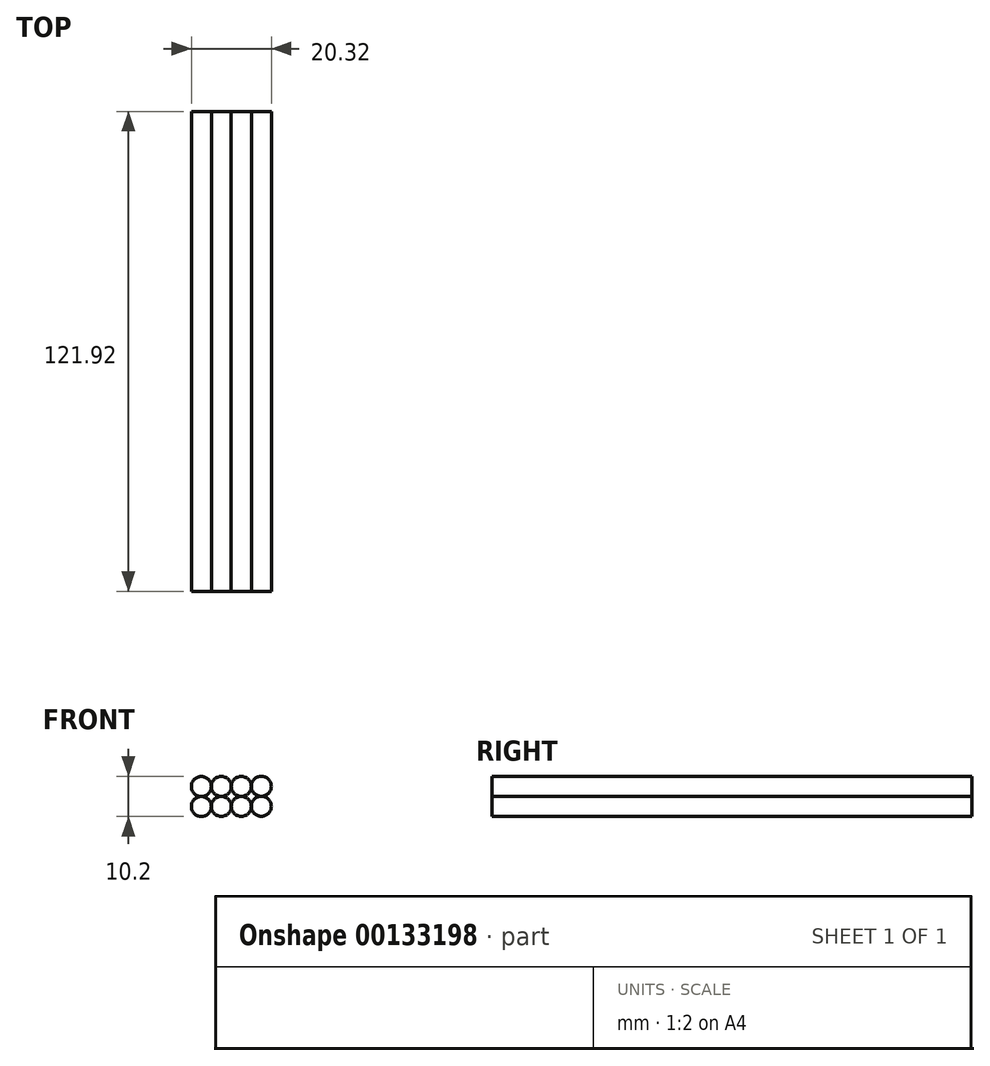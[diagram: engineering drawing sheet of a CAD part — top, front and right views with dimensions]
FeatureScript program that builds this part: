
annotation { "Feature Type Name" : "Feature", "Feature Type Description" : "" }
export const myFeature = defineFeature(function(context is Context, id is Id, definition is map)
    precondition{}
    {
        {
            var Q0;
            Q0=qCreatedBy(makeId("Front.planeOp"),FACE);
            var sketch = newSketch(context, id + "F0", { "sketchPlane" : qUnion([Q0])});
            skCircle(sketch, "E0", {"center": v(0, 0) * mm, "radius": 2.54 * mm});
            skCircle(sketch, "E1.0.1.0", {"center": v(0, 5.08) * mm, "radius": 2.54 * mm});
            skCircle(sketch, "E1.1.0.0", {"center": v(5.08, 0.01) * mm, "radius": 2.54 * mm});
            skCircle(sketch, "E1.1.1.0", {"center": v(5.08, 5.1) * mm, "radius": 2.54 * mm});
            skCircle(sketch, "E1.2.0.0", {"center": v(10.16, 0.02) * mm, "radius": 2.54 * mm});
            skCircle(sketch, "E1.2.1.0", {"center": v(10.16, 5.1) * mm, "radius": 2.54 * mm});
            skCircle(sketch, "E1.3.0.0", {"center": v(15.24, 0.04) * mm, "radius": 2.54 * mm});
            skCircle(sketch, "E1.3.1.0", {"center": v(15.24, 5.12) * mm, "radius": 2.54 * mm});
            skLineSegment(sketch, "E1.direction1", {"start": v(0, 0) * mm, "end": v(5.08, 0.01) * mm, "construction": true});
            skLineSegment(sketch, "E1.direction2", {"start": v(0, 0) * mm, "end": v(0, 5.08) * mm, "construction": true});
            skSolve(sketch);
        }
        {
            var Q0;
            {var subQ0=sQuery(id+"F0.wireOp",EDGE,"E0");var subQ1=makeQuery(id+"F0.imprint","INTERSECT",VERTEX,{"derivedFrom":[subQ0,sQuery(id+"F0.wireOp",EDGE,"E1.0.1.0")]});Q0=makeQuery(id+"F0.imprint","IMPRINT",FACE,{"disambiguationData":[TD([[makeQuery(id+"F0.imprint","IMPRINT",EDGE,{"disambiguationData":[TD([[subQ1,1.0]])],"derivedFrom":subQ0}),1.0]])]});}
            var Q1;
            {var subQ0=sQuery(id+"F0.wireOp",EDGE,"E1.0.1.0");var subQ1=makeQuery(id+"F0.imprint","INTERSECT",VERTEX,{"derivedFrom":[sQuery(id+"F0.wireOp",EDGE,"E0"),subQ0]});Q1=makeQuery(id+"F0.imprint","IMPRINT",FACE,{"disambiguationData":[TD([[makeQuery(id+"F0.imprint","IMPRINT",EDGE,{"disambiguationData":[TD([[subQ1,1.0]])],"derivedFrom":subQ0}),1.0]])]});}
            var Q2;
            {var subQ0=sQuery(id+"F0.wireOp",EDGE,"E1.3.0.0");var subQ1=makeQuery(id+"F0.imprint","INTERSECT",VERTEX,{"derivedFrom":[sQuery(id+"F0.wireOp",EDGE,"E1.2.0.0"),subQ0]});Q2=makeQuery(id+"F0.imprint","IMPRINT",FACE,{"disambiguationData":[TD([[makeQuery(id+"F0.imprint","IMPRINT",EDGE,{"disambiguationData":[TD([[subQ1,1.0]])],"derivedFrom":subQ0}),1.0]])]});}
            var Q3;
            {var subQ0=sQuery(id+"F0.wireOp",EDGE,"E1.3.1.0");var subQ1=makeQuery(id+"F0.imprint","INTERSECT",VERTEX,{"derivedFrom":[sQuery(id+"F0.wireOp",EDGE,"E1.2.1.0"),subQ0]});Q3=makeQuery(id+"F0.imprint","IMPRINT",FACE,{"disambiguationData":[TD([[makeQuery(id+"F0.imprint","IMPRINT",EDGE,{"disambiguationData":[TD([[subQ1,-1.0]])],"derivedFrom":subQ0}),1.0]])]});}
            var Q4;
            {var subQ0=sQuery(id+"F0.wireOp",EDGE,"E1.1.0.0");var subQ1=makeQuery(id+"F0.imprint","INTERSECT",VERTEX,{"derivedFrom":[subQ0,sQuery(id+"F0.wireOp",EDGE,"E1.2.0.0")]});Q4=makeQuery(id+"F0.imprint","IMPRINT",FACE,{"disambiguationData":[TD([[makeQuery(id+"F0.imprint","IMPRINT",EDGE,{"disambiguationData":[TD([[subQ1,-1.0]])],"derivedFrom":subQ0}),1.0]])]});}
            var Q5;
            {var subQ0=sQuery(id+"F0.wireOp",EDGE,"E1.1.1.0");var subQ1=makeQuery(id+"F0.imprint","INTERSECT",VERTEX,{"derivedFrom":[sQuery(id+"F0.wireOp",EDGE,"E1.0.1.0"),subQ0]});Q5=makeQuery(id+"F0.imprint","IMPRINT",FACE,{"disambiguationData":[TD([[makeQuery(id+"F0.imprint","IMPRINT",EDGE,{"disambiguationData":[TD([[subQ1,1.0]])],"derivedFrom":subQ0}),1.0]])]});}
            var Q6;
            {var subQ0=sQuery(id+"F0.wireOp",EDGE,"E1.2.0.0");var subQ1=makeQuery(id+"F0.imprint","INTERSECT",VERTEX,{"derivedFrom":[subQ0,sQuery(id+"F0.wireOp",EDGE,"E1.3.0.0")]});Q6=makeQuery(id+"F0.imprint","IMPRINT",FACE,{"disambiguationData":[TD([[makeQuery(id+"F0.imprint","IMPRINT",EDGE,{"disambiguationData":[TD([[subQ1,-1.0]])],"derivedFrom":subQ0}),1.0]])]});}
            var Q7;
            {var subQ0=sQuery(id+"F0.wireOp",EDGE,"E1.2.1.0");var subQ1=makeQuery(id+"F0.imprint","INTERSECT",VERTEX,{"derivedFrom":[sQuery(id+"F0.wireOp",EDGE,"E1.1.1.0"),subQ0]});Q7=makeQuery(id+"F0.imprint","IMPRINT",FACE,{"disambiguationData":[TD([[makeQuery(id+"F0.imprint","IMPRINT",EDGE,{"disambiguationData":[TD([[subQ1,1.0]])],"derivedFrom":subQ0}),1.0]])]});}
            extrude(context, id + "F1", {"entities" : qUnion([Q0, Q1, Q2, Q3, Q4, Q5, Q6, Q7]), "depth" : 121.92 * mm});
        }
    });
